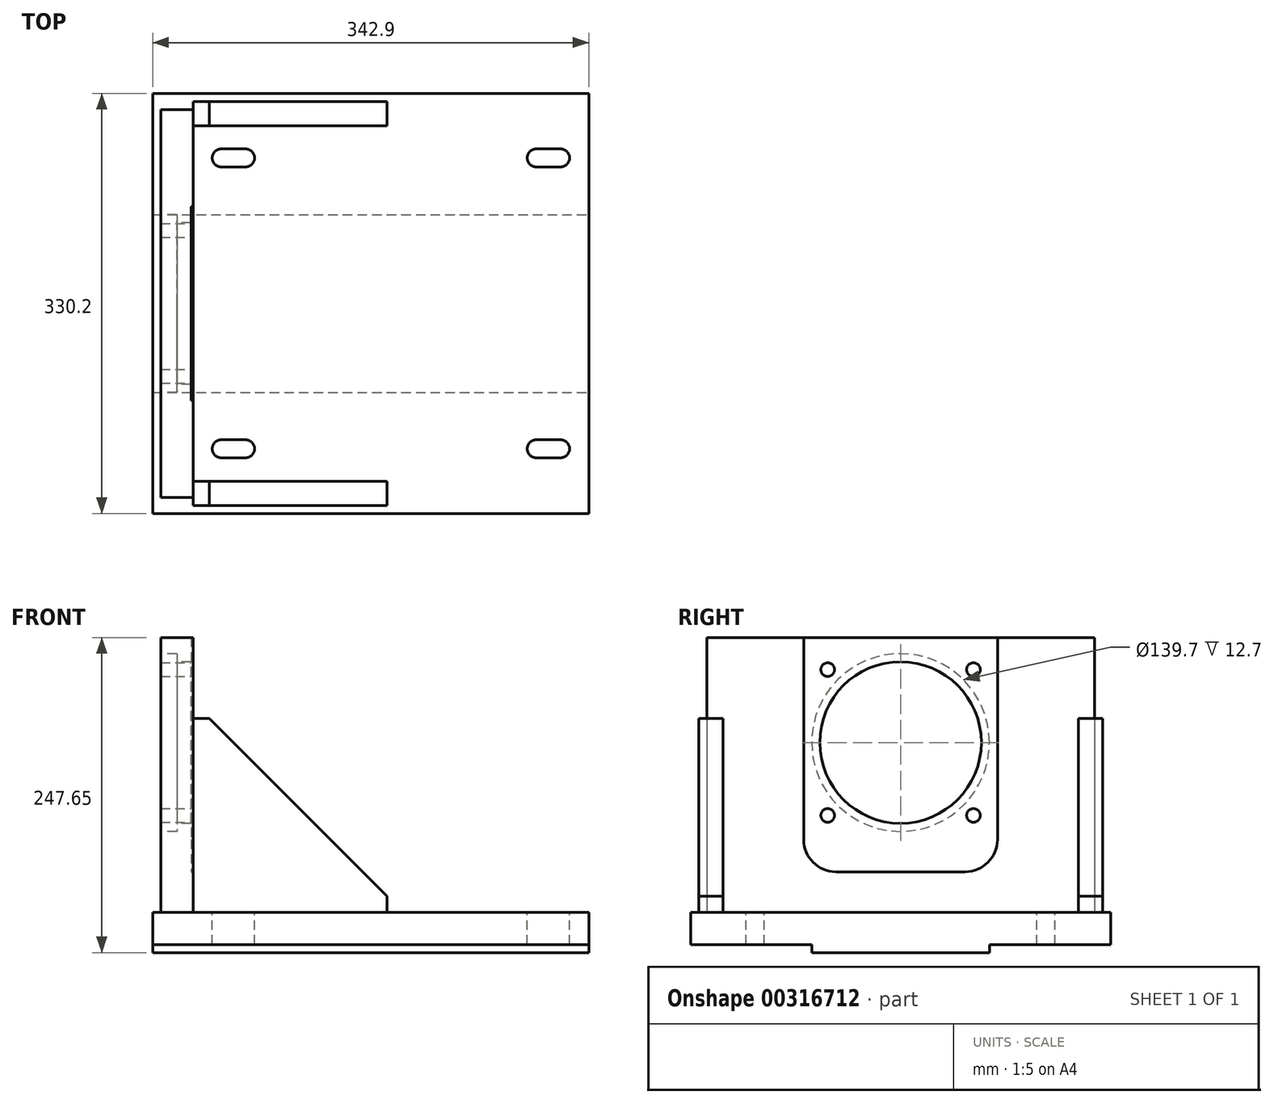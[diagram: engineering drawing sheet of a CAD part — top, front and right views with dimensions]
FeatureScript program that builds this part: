
annotation { "Feature Type Name" : "Feature", "Feature Type Description" : "" }
export const myFeature = defineFeature(function(context is Context, id is Id, definition is map)
    precondition{}
    {
        {
            var Q0;
            Q0=qCreatedBy(makeId("Top.planeOp"),FACE);
            var sketch = newSketch(context, id + "F0", { "sketchPlane" : qUnion([Q0])});
            skLineSegment(sketch, "E0.bottom", {"start": v(-171.45, 165.1) * mm, "end": v(171.45, 165.1) * mm});
            skLineSegment(sketch, "E0.top", {"start": v(-171.45, -165.1) * mm, "end": v(171.45, -165.1) * mm});
            skLineSegment(sketch, "E0.left", {"start": v(-171.45, 165.1) * mm, "end": v(-171.45, -165.1) * mm});
            skLineSegment(sketch, "E0.right", {"start": v(171.45, 165.1) * mm, "end": v(171.45, -165.1) * mm});
            skPoint(sketch, "E0.middle", {"position": v(0, 0) * mm});
            skLineSegment(sketch, "E1.0", {"start": v(149.23, 165.1) * mm, "end": v(149.22, -165.1) * mm, "construction": true});
            skLineSegment(sketch, "E2.0", {"start": v(130.18, 165.1) * mm, "end": v(130.17, -165.1) * mm, "construction": true});
            skLineSegment(sketch, "E3", {"start": v(-287.48, 0) * mm, "end": v(272.76, 0) * mm, "construction": true});
            skPoint(sketch, "E3.endSnap0", {"position": v(171.45, 0) * mm});
            skLineSegment(sketch, "E4.0", {"start": v(-287.48, -114.3) * mm, "end": v(-171.45, -114.3) * mm, "construction": true});
            skLineSegment(sketch, "E5.0", {"start": v(-98.42, 165.1) * mm, "end": v(-98.43, -165.1) * mm, "construction": true});
            skLineSegment(sketch, "E6.0", {"start": v(-117.47, 165.1) * mm, "end": v(-117.48, -165.1) * mm, "construction": true});
            skLineSegment(sketch, "E7.trimOffspring", {"start": v(-117.48, -114.3) * mm, "end": v(-98.43, -114.3) * mm});
            skLineSegment(sketch, "E8.trimOffspring", {"start": v(130.17, -114.3) * mm, "end": v(149.22, -114.3) * mm});
            skLineSegment(sketch, "E9.trimOffspring", {"start": v(171.45, -114.3) * mm, "end": v(272.76, -114.3) * mm, "construction": true});
            skArc(sketch, "E10.0.startCap", {"start": v(-117.48, -121.41) * mm, "mid": v(-124.59, -114.3) * mm, "end": v(-117.48, -107.19) * mm});
            skArc(sketch, "E10.0.endCap", {"start": v(-98.43, -107.19) * mm, "mid": v(-91.31, -114.3) * mm, "end": v(-98.43, -121.41) * mm});
            skLineSegment(sketch, "E10.0.left", {"start": v(-117.48, -107.19) * mm, "end": v(-98.43, -107.19) * mm});
            skLineSegment(sketch, "E10.0.right", {"start": v(-117.48, -121.41) * mm, "end": v(-98.43, -121.41) * mm});
            skArc(sketch, "E10.1.startCap", {"start": v(130.17, -121.41) * mm, "mid": v(123.06, -114.3) * mm, "end": v(130.17, -107.19) * mm});
            skArc(sketch, "E10.1.endCap", {"start": v(149.22, -107.19) * mm, "mid": v(156.34, -114.3) * mm, "end": v(149.22, -121.41) * mm});
            skLineSegment(sketch, "E10.1.left", {"start": v(130.17, -107.19) * mm, "end": v(149.22, -107.19) * mm});
            skLineSegment(sketch, "E10.1.right", {"start": v(130.17, -121.41) * mm, "end": v(149.22, -121.41) * mm});
            skLineSegment(sketch, "E11.MirrorCS", {"start": v(-117.48, 114.3) * mm, "end": v(-98.43, 114.3) * mm});
            skLineSegment(sketch, "E12.MirrorCS", {"start": v(-117.48, 107.19) * mm, "end": v(-98.43, 107.19) * mm});
            skLineSegment(sketch, "E13.MirrorCS", {"start": v(130.17, 107.19) * mm, "end": v(149.22, 107.19) * mm});
            skLineSegment(sketch, "E14.MirrorCS", {"start": v(130.17, 114.3) * mm, "end": v(149.22, 114.3) * mm});
            skLineSegment(sketch, "E15.MirrorCS", {"start": v(130.17, 121.41) * mm, "end": v(149.22, 121.41) * mm});
            skArc(sketch, "E16.MirrorCS", {"start": v(-117.48, 121.41) * mm, "mid": v(-124.59, 114.3) * mm, "end": v(-117.48, 107.19) * mm});
            skArc(sketch, "E17.MirrorCS", {"start": v(130.18, 121.41) * mm, "mid": v(123.06, 114.3) * mm, "end": v(130.18, 107.19) * mm});
            skLineSegment(sketch, "E18.MirrorCS", {"start": v(-117.48, 121.41) * mm, "end": v(-98.43, 121.41) * mm});
            skArc(sketch, "E19.MirrorCS", {"start": v(-98.43, 107.19) * mm, "mid": v(-91.31, 114.3) * mm, "end": v(-98.43, 121.41) * mm});
            skArc(sketch, "E20.MirrorCS", {"start": v(149.23, 107.19) * mm, "mid": v(156.34, 114.3) * mm, "end": v(149.23, 121.41) * mm});
            skSolve(sketch);
        }
        {
            var Q0;
            Q0 = qSketchRegion(id + "F0", true);
            extrude(context, id + "F1", {"entities" : qUnion([Q0]), "oppositeDirection" : true, "depth" : 25.4 * mm});
        }
        {
            var Q0;
            Q0=makeQuery(id+"F1.opExtrude","CAP_FACE",FACE,{"disambiguationData":[OSD([sQuery(id+"F0.wireOp",EDGE,"E0.bottom"),sQuery(id+"F0.wireOp",EDGE,"E0.top"),sQuery(id+"F0.wireOp",EDGE,"E0.left"),sQuery(id+"F0.wireOp",EDGE,"E0.right"),sQuery(id+"F0.wireOp",EDGE,"E10.0.startCap"),sQuery(id+"F0.wireOp",EDGE,"E10.0.endCap"),sQuery(id+"F0.wireOp",EDGE,"E10.0.left"),sQuery(id+"F0.wireOp",EDGE,"E10.0.right"),sQuery(id+"F0.wireOp",EDGE,"E10.1.startCap"),sQuery(id+"F0.wireOp",EDGE,"E10.1.endCap"),sQuery(id+"F0.wireOp",EDGE,"E10.1.left"),sQuery(id+"F0.wireOp",EDGE,"E10.1.right"),sQuery(id+"F0.wireOp",EDGE,"E12.MirrorCS"),sQuery(id+"F0.wireOp",EDGE,"E13.MirrorCS"),sQuery(id+"F0.wireOp",EDGE,"E15.MirrorCS"),sQuery(id+"F0.wireOp",EDGE,"E16.MirrorCS"),sQuery(id+"F0.wireOp",EDGE,"E17.MirrorCS"),sQuery(id+"F0.wireOp",EDGE,"E18.MirrorCS"),sQuery(id+"F0.wireOp",EDGE,"E19.MirrorCS"),sQuery(id+"F0.wireOp",EDGE,"E20.MirrorCS")])],"isStart":false});
            var sketch = newSketch(context, id + "F2", { "sketchPlane" : qUnion([Q0])});
            skLineSegment(sketch, "E21.bottom", {"start": v(-171.45, 69.85) * mm, "end": v(171.45, 69.85) * mm});
            skLineSegment(sketch, "E21.top", {"start": v(-171.45, -69.85) * mm, "end": v(171.45, -69.85) * mm});
            skLineSegment(sketch, "E21.left", {"start": v(-171.45, 69.85) * mm, "end": v(-171.45, -69.85) * mm});
            skLineSegment(sketch, "E21.right", {"start": v(171.45, 69.85) * mm, "end": v(171.45, -69.85) * mm});
            skPoint(sketch, "E21.middle", {"position": v(0, 0) * mm});
            skSolve(sketch);
        }
        {
            var Q0;
            Q0 = qSketchRegion(id + "F2", true);
            extrude(context, id + "F3", {"entities" : qUnion([Q0]), "operationType" : NewBodyOperationType.ADD, "depth" : 6.35 * mm});
        }
        {
            var Q0;
            Q0=makeQuery(id+"F1.opExtrude","CAP_FACE",FACE,{"disambiguationData":[OSD([sQuery(id+"F0.wireOp",EDGE,"E0.bottom"),sQuery(id+"F0.wireOp",EDGE,"E0.top"),sQuery(id+"F0.wireOp",EDGE,"E0.left"),sQuery(id+"F0.wireOp",EDGE,"E0.right"),sQuery(id+"F0.wireOp",EDGE,"E10.0.startCap"),sQuery(id+"F0.wireOp",EDGE,"E10.0.endCap"),sQuery(id+"F0.wireOp",EDGE,"E10.0.left"),sQuery(id+"F0.wireOp",EDGE,"E10.0.right"),sQuery(id+"F0.wireOp",EDGE,"E10.1.startCap"),sQuery(id+"F0.wireOp",EDGE,"E10.1.endCap"),sQuery(id+"F0.wireOp",EDGE,"E10.1.left"),sQuery(id+"F0.wireOp",EDGE,"E10.1.right"),sQuery(id+"F0.wireOp",EDGE,"E12.MirrorCS"),sQuery(id+"F0.wireOp",EDGE,"E13.MirrorCS"),sQuery(id+"F0.wireOp",EDGE,"E15.MirrorCS"),sQuery(id+"F0.wireOp",EDGE,"E16.MirrorCS"),sQuery(id+"F0.wireOp",EDGE,"E17.MirrorCS"),sQuery(id+"F0.wireOp",EDGE,"E18.MirrorCS"),sQuery(id+"F0.wireOp",EDGE,"E19.MirrorCS"),sQuery(id+"F0.wireOp",EDGE,"E20.MirrorCS")])],"isStart":true});
            var sketch = newSketch(context, id + "F4", { "sketchPlane" : qUnion([Q0])});
            skLineSegment(sketch, "E22.0", {"start": v(-165.1, 152.4) * mm, "end": v(-165.1, -152.4) * mm});
            skLineSegment(sketch, "E23.0", {"start": v(-139.7, 152.4) * mm, "end": v(-139.7, -152.4) * mm});
            skLineSegment(sketch, "E24", {"start": v(-299.95, 0) * mm, "end": v(210.66, 0) * mm, "construction": true});
            skLineSegment(sketch, "E25.0", {"start": v(-165.1, -152.4) * mm, "end": v(-139.7, -152.4) * mm});
            skLineSegment(sketch, "E26.MirrorCS", {"start": v(-165.1, 152.4) * mm, "end": v(-139.7, 152.4) * mm});
            skSolve(sketch);
        }
        {
            var Q0;
            Q0 = qSketchRegion(id + "F4", true);
            extrude(context, id + "F5", {"entities" : qUnion([Q0]), "operationType" : NewBodyOperationType.ADD, "depth" : 215.9 * mm});
        }
        {
            var Q0;
            Q0=makeQuery(id+"F5.opExtrude","SWEPT_FACE",FACE,{"disambiguationData":[OSD([sQuery(id+"F4.wireOp",EDGE,"E22.0")])]});
            var sketch = newSketch(context, id + "F6", { "sketchPlane" : qUnion([Q0])});
            skLineSegment(sketch, "E27.0", {"start": v(-152.4, 133.35) * mm, "end": v(152.4, 133.35) * mm, "construction": true});
            skPoint(sketch, "E28", {"position": v(0, 133.35) * mm});
            skSolve(sketch);
        }
        {
            var Q0;
            Q0=sQuery(id+"F6.wireOp",VERTEX,"E28");
            var Q1;
            Q1=makeQuery(id+"F1.opExtrude","SWEPT_BODY",BODY,{"disambiguationData":[OSD([sQuery(id+"F0.wireOp",EDGE,"E0.bottom"),sQuery(id+"F0.wireOp",EDGE,"E0.top"),sQuery(id+"F0.wireOp",EDGE,"E0.left"),sQuery(id+"F0.wireOp",EDGE,"E0.right"),sQuery(id+"F0.wireOp",EDGE,"E10.0.startCap"),sQuery(id+"F0.wireOp",EDGE,"E10.0.endCap"),sQuery(id+"F0.wireOp",EDGE,"E10.0.left"),sQuery(id+"F0.wireOp",EDGE,"E10.0.right"),sQuery(id+"F0.wireOp",EDGE,"E10.1.startCap"),sQuery(id+"F0.wireOp",EDGE,"E10.1.endCap"),sQuery(id+"F0.wireOp",EDGE,"E10.1.left"),sQuery(id+"F0.wireOp",EDGE,"E10.1.right"),sQuery(id+"F0.wireOp",EDGE,"E12.MirrorCS"),sQuery(id+"F0.wireOp",EDGE,"E13.MirrorCS"),sQuery(id+"F0.wireOp",EDGE,"E15.MirrorCS"),sQuery(id+"F0.wireOp",EDGE,"E16.MirrorCS"),sQuery(id+"F0.wireOp",EDGE,"E17.MirrorCS"),sQuery(id+"F0.wireOp",EDGE,"E18.MirrorCS"),sQuery(id+"F0.wireOp",EDGE,"E19.MirrorCS"),sQuery(id+"F0.wireOp",EDGE,"E20.MirrorCS")])]});
            hole(context, id + "F7", {"style" : HoleStyle.C_BORE, "endStyle" : HoleEndStyle.THROUGH, "holeDiameter" : 127 * mm, "cBoreDiameter" : 139.7 * mm, "cBoreDepth" : 12.7 * mm, "tappedDepth" : 10 * mm, "tapClearance" : 3, "locations" : qUnion([Q0]), "scope" : qUnion([Q1])});
        }
        {
            var Q0;
            Q0=makeQuery(id+"F5.opExtrude","SWEPT_FACE",FACE,{"disambiguationData":[OSD([sQuery(id+"F4.wireOp",EDGE,"E23.0")])]});
            var sketch = newSketch(context, id + "F8", { "sketchPlane" : qUnion([Q0])});
            skCircle(sketch, "E29.0", {"center": v(0, 133.35) * mm, "radius": 63.5 * mm, "construction": true});
            skLineSegment(sketch, "E30.0", {"start": v(50.8, 31.75) * mm, "end": v(-50.8, 31.75) * mm});
            skLineSegment(sketch, "E31", {"start": v(0, 360.03) * mm, "end": v(0, -161.05) * mm});
            skLineSegment(sketch, "E32.0", {"start": v(-76.2, 360.03) * mm, "end": v(-76.2, 57.15) * mm});
            skLineSegment(sketch, "E33.0", {"start": v(152.4, 215.9) * mm, "end": v(-152.4, 215.9) * mm});
            skLineSegment(sketch, "E34.MirrorCS", {"start": v(76.2, 360.03) * mm, "end": v(76.2, 57.15) * mm});
            skPoint(sketch, "E35.newPointA", {"position": v(76.2, -161.05) * mm});
            skArc(sketch, "E35.filletArc", {"start": v(50.8, 31.75) * mm, "mid": v(68.76, 39.19) * mm, "end": v(76.2, 57.15) * mm});
            skPoint(sketch, "E36.newPointB", {"position": v(-76.2, -161.05) * mm});
            skArc(sketch, "E36.filletArc", {"start": v(-76.2, 57.15) * mm, "mid": v(-68.76, 39.19) * mm, "end": v(-50.8, 31.75) * mm});
            skSolve(sketch);
        }
        {
            var Q0;
            Q0 = qSketchRegion(id + "F8", true);
            extrude(context, id + "F9", {"entities" : qUnion([Q0]), "operationType" : NewBodyOperationType.REMOVE, "oppositeDirection" : true, "depth" : 1.52 * mm});
        }
        {
            var Q0;
            Q0=makeQuery(id+"F9.boolean.opBoolean","COPY",FACE,{"derivedFrom":makeQuery(id+"F9.opExtrude","CAP_FACE",FACE,{"disambiguationData":[OSD([sQuery(id+"F8.wireOp",EDGE,"E30.0"),sQuery(id+"F8.wireOp",EDGE,"E32.0"),sQuery(id+"F8.wireOp",EDGE,"E33.0"),sQuery(id+"F8.wireOp",EDGE,"E34.MirrorCS"),sQuery(id+"F8.wireOp",EDGE,"E35.filletArc"),sQuery(id+"F8.wireOp",EDGE,"E36.filletArc")])],"isStart":false})});
            var sketch = newSketch(context, id + "F10", { "sketchPlane" : qUnion([Q0])});
            skCircle(sketch, "E37.0", {"center": v(0, 133.35) * mm, "radius": 63.5 * mm, "construction": true});
            skCircle(sketch, "E38", {"center": v(0, 133.35) * mm, "radius": 81.03 * mm, "construction": true});
            skLineSegment(sketch, "E39", {"start": v(0, 133.35) * mm, "end": v(0, 285.7) * mm, "construction": true});
            skLineSegment(sketch, "E40", {"start": v(0, 133.35) * mm, "end": v(155.7, 289.05) * mm, "construction": true});
            skPoint(sketch, "E41", {"position": v(57.3, 190.64) * mm});
            skPoint(sketch, "E42.1.0", {"position": v(-57.3, 190.64) * mm});
            skPoint(sketch, "E42.2.0", {"position": v(-57.3, 76.06) * mm});
            skPoint(sketch, "E42.3.0", {"position": v(57.3, 76.06) * mm});
            skSolve(sketch);
        }
        {
            var Q0;
            Q0=sQuery(id+"F10.wireOp",VERTEX,"E41");
            var Q1;
            Q1=sQuery(id+"F10.wireOp",VERTEX,"E42.3.0");
            var Q2;
            Q2=sQuery(id+"F10.wireOp",VERTEX,"E42.2.0");
            var Q3;
            Q3=sQuery(id+"F10.wireOp",VERTEX,"E42.1.0");
            var Q4;
            Q4=makeQuery(id+"F1.opExtrude","SWEPT_BODY",BODY,{"disambiguationData":[OSD([sQuery(id+"F0.wireOp",EDGE,"E0.bottom"),sQuery(id+"F0.wireOp",EDGE,"E0.top"),sQuery(id+"F0.wireOp",EDGE,"E0.left"),sQuery(id+"F0.wireOp",EDGE,"E0.right"),sQuery(id+"F0.wireOp",EDGE,"E10.0.startCap"),sQuery(id+"F0.wireOp",EDGE,"E10.0.endCap"),sQuery(id+"F0.wireOp",EDGE,"E10.0.left"),sQuery(id+"F0.wireOp",EDGE,"E10.0.right"),sQuery(id+"F0.wireOp",EDGE,"E10.1.startCap"),sQuery(id+"F0.wireOp",EDGE,"E10.1.endCap"),sQuery(id+"F0.wireOp",EDGE,"E10.1.left"),sQuery(id+"F0.wireOp",EDGE,"E10.1.right"),sQuery(id+"F0.wireOp",EDGE,"E12.MirrorCS"),sQuery(id+"F0.wireOp",EDGE,"E13.MirrorCS"),sQuery(id+"F0.wireOp",EDGE,"E15.MirrorCS"),sQuery(id+"F0.wireOp",EDGE,"E16.MirrorCS"),sQuery(id+"F0.wireOp",EDGE,"E17.MirrorCS"),sQuery(id+"F0.wireOp",EDGE,"E18.MirrorCS"),sQuery(id+"F0.wireOp",EDGE,"E19.MirrorCS"),sQuery(id+"F0.wireOp",EDGE,"E20.MirrorCS")])]});
            hole(context, id + "F11", {"style" : HoleStyle.SIMPLE, "endStyle" : HoleEndStyle.THROUGH, "standardTappedOrClearance" : lookupTablePath({ "standard" : "ANSI", "engagement" : "75%", "pitch" : "13 tpi", "size" : "1/2", "type" : "Tapped" }), "standardBlindInLast" : lookupTablePath({ "standard" : "ANSI", "engagement" : "75%", "pitch" : "13 tpi", "size" : "1/2", "type" : "Tapped" }), "holeDiameter" : 10.72 * mm, "showTappedDepth" : true, "tappedDepth" : 10 * mm, "tapClearance" : 3, "locations" : qUnion([Q0, Q1, Q2, Q3]), "scope" : qUnion([Q4]), "majorDiameter" : 12.7 * mm});
        }
        {
            var Q0;
            Q0=makeQuery(id+"F1.opExtrude","CAP_FACE",FACE,{"disambiguationData":[OSD([sQuery(id+"F0.wireOp",EDGE,"E0.bottom"),sQuery(id+"F0.wireOp",EDGE,"E0.top"),sQuery(id+"F0.wireOp",EDGE,"E0.left"),sQuery(id+"F0.wireOp",EDGE,"E0.right"),sQuery(id+"F0.wireOp",EDGE,"E10.0.startCap"),sQuery(id+"F0.wireOp",EDGE,"E10.0.endCap"),sQuery(id+"F0.wireOp",EDGE,"E10.0.left"),sQuery(id+"F0.wireOp",EDGE,"E10.0.right"),sQuery(id+"F0.wireOp",EDGE,"E10.1.startCap"),sQuery(id+"F0.wireOp",EDGE,"E10.1.endCap"),sQuery(id+"F0.wireOp",EDGE,"E10.1.left"),sQuery(id+"F0.wireOp",EDGE,"E10.1.right"),sQuery(id+"F0.wireOp",EDGE,"E12.MirrorCS"),sQuery(id+"F0.wireOp",EDGE,"E13.MirrorCS"),sQuery(id+"F0.wireOp",EDGE,"E15.MirrorCS"),sQuery(id+"F0.wireOp",EDGE,"E16.MirrorCS"),sQuery(id+"F0.wireOp",EDGE,"E17.MirrorCS"),sQuery(id+"F0.wireOp",EDGE,"E18.MirrorCS"),sQuery(id+"F0.wireOp",EDGE,"E19.MirrorCS"),sQuery(id+"F0.wireOp",EDGE,"E20.MirrorCS")])],"isStart":true});
            var sketch = newSketch(context, id + "F12", { "sketchPlane" : qUnion([Q0])});
            skLineSegment(sketch, "E43.0", {"start": v(-139.7, 158.75) * mm, "end": v(12.7, 158.75) * mm});
            skLineSegment(sketch, "E44.0", {"start": v(12.7, 158.75) * mm, "end": v(12.7, 139.7) * mm});
            skLineSegment(sketch, "E45.0", {"start": v(-139.7, 139.7) * mm, "end": v(12.7, 139.7) * mm});
            skPoint(sketch, "E46.0", {"position": v(-139.7, 114.3) * mm});
            skLineSegment(sketch, "E47.0", {"start": v(-139.7, 158.75) * mm, "end": v(-139.7, 139.7) * mm});
            skPoint(sketch, "E48.orphan", {"position": v(-139.7, 152.4) * mm});
            skPoint(sketch, "E49.orphan", {"position": v(-139.7, 76.2) * mm});
            skLineSegment(sketch, "E50", {"start": v(-224.57, 0) * mm, "end": v(197.35, 0) * mm, "construction": true});
            skLineSegment(sketch, "E51.MirrorCS", {"start": v(-139.7, -158.75) * mm, "end": v(-139.7, -139.7) * mm});
            skPoint(sketch, "E52.MirrorP", {"position": v(-139.7, -152.4) * mm});
            skLineSegment(sketch, "E53.MirrorCS", {"start": v(-139.7, -158.75) * mm, "end": v(12.7, -158.75) * mm});
            skPoint(sketch, "E54.MirrorP", {"position": v(-139.7, -114.3) * mm});
            skLineSegment(sketch, "E55.MirrorCS", {"start": v(12.7, -158.75) * mm, "end": v(12.7, -139.7) * mm});
            skLineSegment(sketch, "E56.MirrorCS", {"start": v(-139.7, -139.7) * mm, "end": v(12.7, -139.7) * mm});
            skSolve(sketch);
        }
        {
            var Q0;
            Q0 = qSketchRegion(id + "F12", true);
            extrude(context, id + "F13", {"entities" : qUnion([Q0]), "operationType" : NewBodyOperationType.ADD, "depth" : 152.4 * mm});
        }
        {
            var Q0;
            Q0=makeQuery(id+"F13.opExtrude","CAP_EDGE",EDGE,{"disambiguationData":[OSD([sQuery(id+"F12.wireOp",EDGE,"E44.0")])],"isStart":false});
            var Q1;
            Q1=makeQuery(id+"F13.opExtrude","CAP_EDGE",EDGE,{"disambiguationData":[OSD([sQuery(id+"F12.wireOp",EDGE,"E55.MirrorCS")])],"isStart":false});
            chamfer(context, id + "F14", {"entities" : qUnion([Q0, Q1]), "width" : 139.7 * mm, "tangentPropagation" : true});
        }
    });
